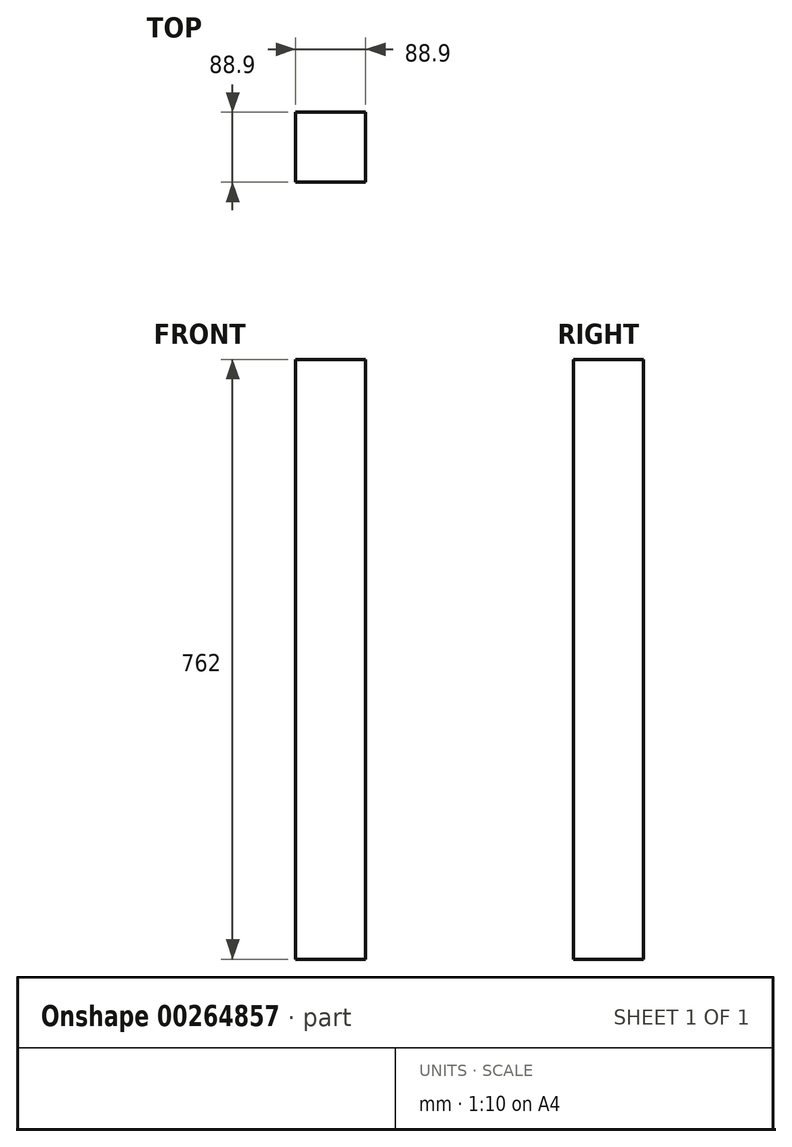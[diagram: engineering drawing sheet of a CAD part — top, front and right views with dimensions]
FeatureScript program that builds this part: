
annotation { "Feature Type Name" : "Feature", "Feature Type Description" : "" }
export const myFeature = defineFeature(function(context is Context, id is Id, definition is map)
    precondition{}
    {
        {
            var Q0;
            Q0=qCreatedBy(makeId("Top.planeOp"),FACE);
            var sketch = newSketch(context, id + "F0", { "sketchPlane" : qUnion([Q0])});
            skLineSegment(sketch, "E0.bottom", {"start": v(0, 0) * mm, "end": v(88.9, 0) * mm});
            skLineSegment(sketch, "E0.top", {"start": v(0, 88.9) * mm, "end": v(88.9, 88.9) * mm});
            skLineSegment(sketch, "E0.left", {"start": v(0, 0) * mm, "end": v(0, 88.9) * mm});
            skLineSegment(sketch, "E0.right", {"start": v(88.9, 0) * mm, "end": v(88.9, 88.9) * mm});
            skSolve(sketch);
        }
        {
            var Q0;
            Q0=makeQuery(id+"F0.imprint","IMPRINT",FACE,{"disambiguationData":[TD([[makeQuery(id+"F0.imprint","IMPRINT",EDGE,{"derivedFrom":sQuery(id+"F0.wireOp",EDGE,"E0.bottom")}),1.0]])]});
            extrude(context, id + "F1", {"entities" : qUnion([Q0]), "depth" : 762 * mm, "offsetDistance" : 25.4 * mm});
        }
    });
